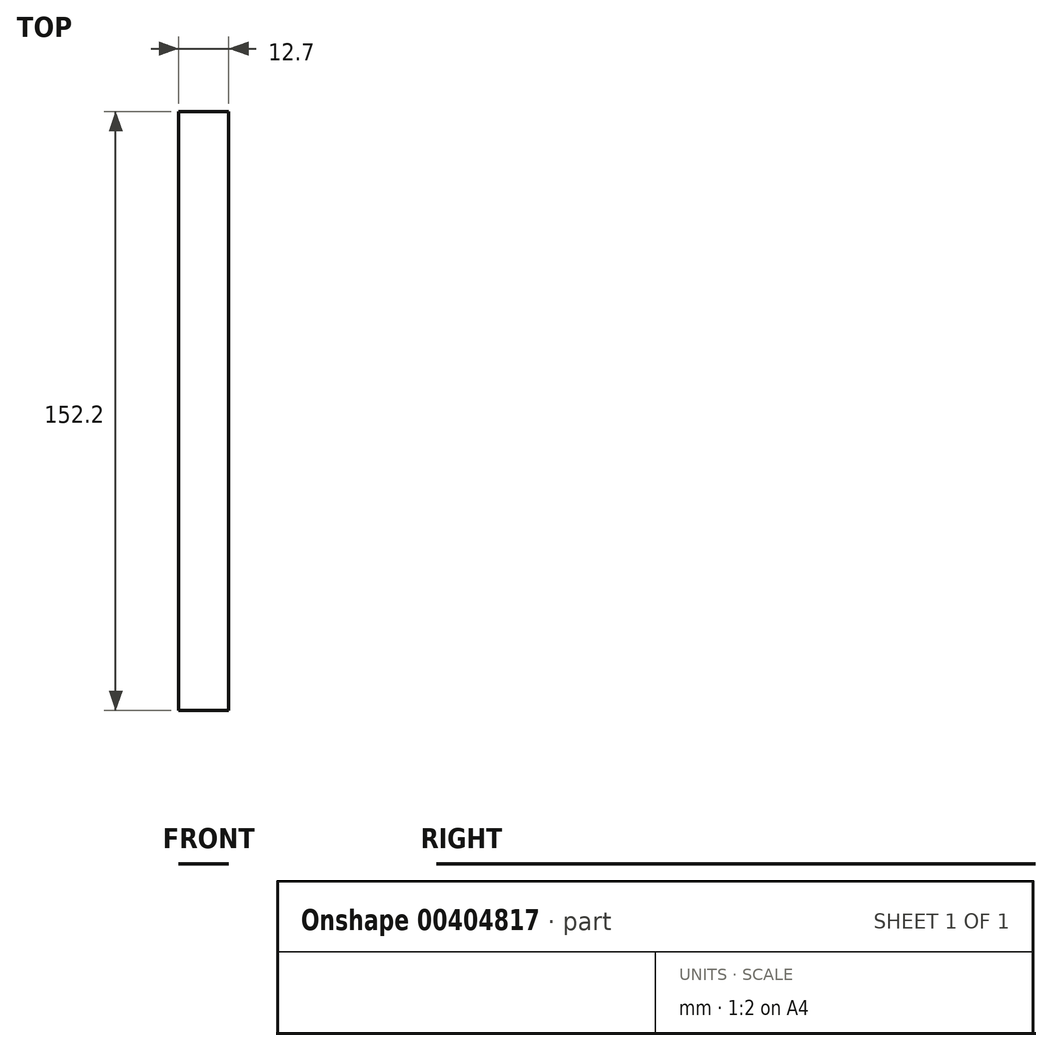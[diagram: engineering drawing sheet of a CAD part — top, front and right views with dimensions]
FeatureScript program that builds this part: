
annotation { "Feature Type Name" : "Feature", "Feature Type Description" : "" }
export const myFeature = defineFeature(function(context is Context, id is Id, definition is map)
    precondition{}
    {
        {
            var Q0;
            Q0=qCreatedBy(makeId("Right.planeOp"),FACE);
            var sketch = newSketch(context, id + "F0", { "sketchPlane" : qUnion([Q0])});
            skLineSegment(sketch, "E0", {"start": v(-76.07, 23.77) * mm, "end": v(-76.07, 0) * mm});
            skLineSegment(sketch, "E1", {"start": v(-76.07, 0) * mm, "end": v(76.13, 0) * mm});
            skLineSegment(sketch, "E2", {"start": v(76.13, 0) * mm, "end": v(76.13, 23.77) * mm});
            skLineSegment(sketch, "E3", {"start": v(76.13, 23.77) * mm, "end": v(-76.07, 23.77) * mm});
            skSolve(sketch);
        }
        {
            var Q0;
            Q0=makeQuery(id+"F0.imprint","IMPRINT",FACE,{"disambiguationData":[TD([[makeQuery(id+"F0.imprint","IMPRINT",EDGE,{"derivedFrom":sQuery(id+"F0.wireOp",EDGE,"E0")}),1.0]])]});
            var Q1;
            Q1=sQuery(id+"F0.wireOp",EDGE,"E1");
            extrude(context, id + "F1", {"entities" : qUnion([Q0]), "bodyType" : ToolBodyType.SURFACE, "surfaceEntities" : qUnion([Q1]), "depth" : 12.7 * mm});
        }
    });
